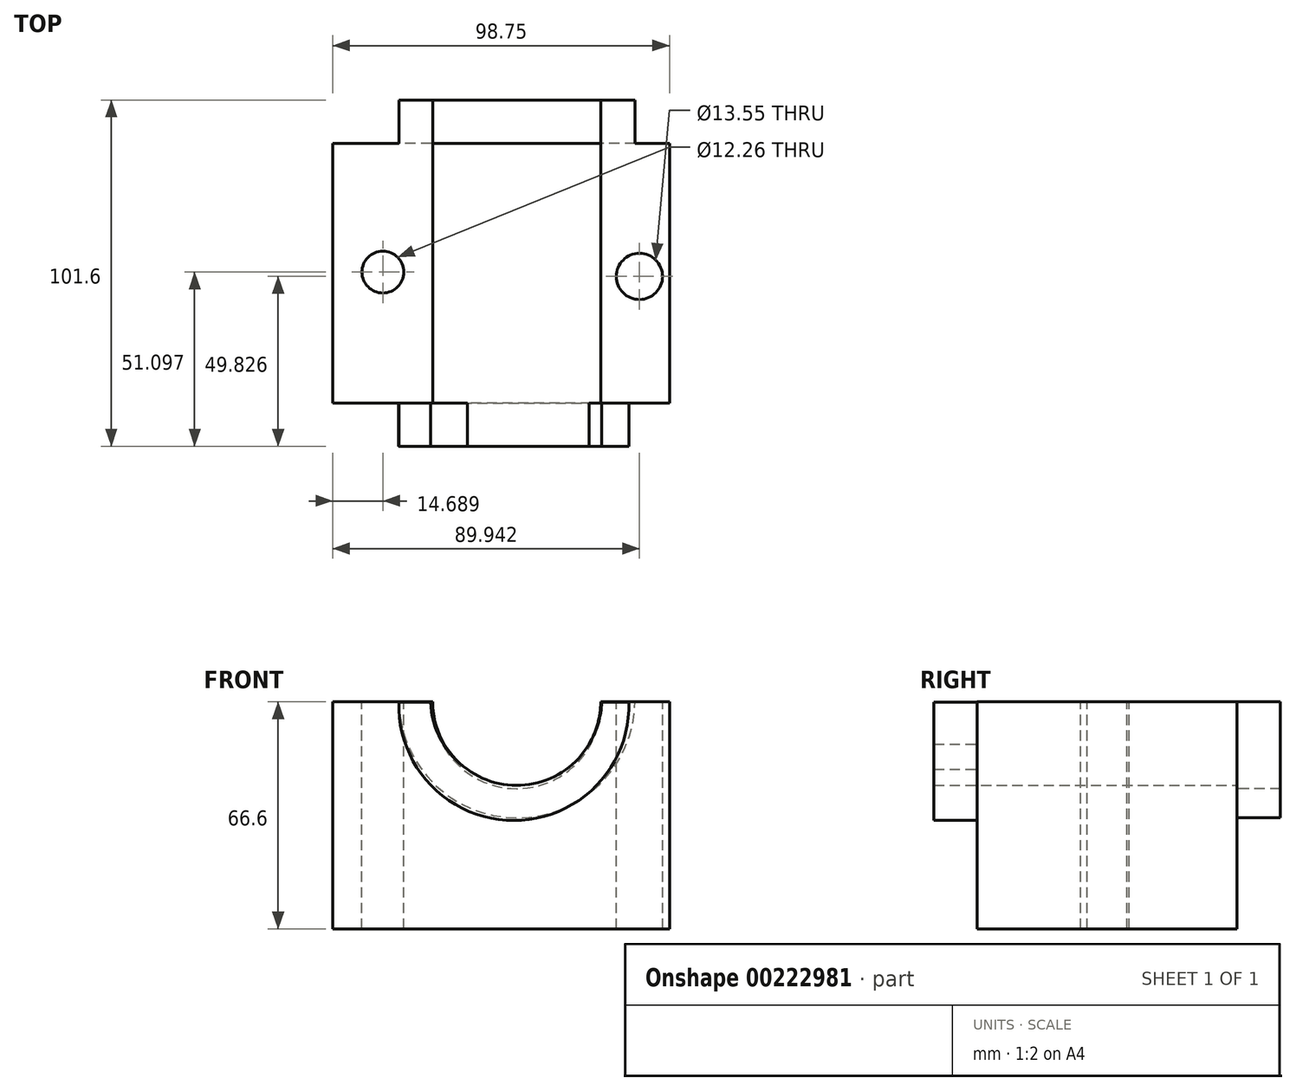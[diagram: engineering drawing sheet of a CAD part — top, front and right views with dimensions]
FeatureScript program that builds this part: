
annotation { "Feature Type Name" : "Feature", "Feature Type Description" : "" }
export const myFeature = defineFeature(function(context is Context, id is Id, definition is map)
    precondition{}
    {
        {
            var Q0;
            Q0=qCreatedBy(makeId("Front.planeOp"),FACE);
            var sketch = newSketch(context, id + "F0", { "sketchPlane" : qUnion([Q0])});
            skLineSegment(sketch, "E0.bottom", {"start": v(32.3, -49.6) * mm, "end": v(-66.44, -49.6) * mm});
            skLineSegment(sketch, "E0.top", {"start": v(32.3, 17) * mm, "end": v(-66.44, 17) * mm});
            skLineSegment(sketch, "E0.left", {"start": v(32.3, -49.6) * mm, "end": v(32.3, 17) * mm});
            skLineSegment(sketch, "E0.right", {"start": v(-66.44, -49.6) * mm, "end": v(-66.44, 17) * mm});
            skSolve(sketch);
        }
        {
            var Q0;
            Q0 = qSketchRegion(id + "F0", true);
            extrude(context, id + "F1", {"entities" : qUnion([Q0]), "oppositeDirection" : true, "depth" : 76.2 * mm});
        }
        {
            var Q0;
            Q0=makeQuery(id+"F1.opExtrude","CAP_FACE",FACE,{"disambiguationData":[OSD([sQuery(id+"F0.wireOp",EDGE,"E0.bottom"),sQuery(id+"F0.wireOp",EDGE,"E0.top"),sQuery(id+"F0.wireOp",EDGE,"E0.left"),sQuery(id+"F0.wireOp",EDGE,"E0.right")])],"isStart":true});
            var sketch = newSketch(context, id + "F2", { "sketchPlane" : qUnion([Q0])});
            skSolve(sketch);
        }
        {
            var Q0;
            Q0=makeQuery(id+"F2.imprint","IMPRINT",FACE,{"disambiguationData":[TD([[makeQuery(id+"F2.imprint","IMPRINT",EDGE,{"derivedFrom":makeQuery(id+"F1.opExtrude","CAP_EDGE",EDGE,{"disambiguationData":[OSD([sQuery(id+"F0.wireOp",EDGE,"E0.bottom")])],"isStart":true})}),-1.0]])]});
            var sketch = newSketch(context, id + "F3", { "sketchPlane" : qUnion([Q0])});
            skLineSegment(sketch, "E1", {"start": v(-37.75, 16.91) * mm, "end": v(-47.07, 16.91) * mm});
            skLineSegment(sketch, "E2", {"start": v(-47.07, 16.91) * mm, "end": v(-37.75, 16.91) * mm});
            skLineSegment(sketch, "E3", {"start": v(12.44, 16.91) * mm, "end": v(20.38, 16.91) * mm});
            skLineSegment(sketch, "E4", {"start": v(20.38, 16.91) * mm, "end": v(12.44, 16.91) * mm});
            skArc(sketch, "E5", {"start": v(-47.07, 16.91) * mm, "mid": v(-13.34, -17.83) * mm, "end": v(20.38, 16.91) * mm});
            skArc(sketch, "E6", {"start": v(-37.75, 16.91) * mm, "mid": v(-12.65, -7.34) * mm, "end": v(12.44, 16.91) * mm});
            skSolve(sketch);
        }
        {
            var Q0;
            Q0 = qSketchRegion(id + "F3", true);
            extrude(context, id + "F4", {"entities" : qUnion([Q0]), "operationType" : NewBodyOperationType.ADD, "depth" : 12.7 * mm});
        }
        {
            var Q0;
            Q0=qCreatedBy(makeId("Front.planeOp"),FACE);
            var sketch = newSketch(context, id + "F5", { "sketchPlane" : qUnion([Q0])});
            skCircle(sketch, "E7", {"center": v(-12.51, 17.09) * mm, "radius": 24.64 * mm});
            skSolve(sketch);
        }
        {
            var Q0;
            Q0 = qSketchRegion(id + "F5", true);
            extrude(context, id + "F6", {"entities" : qUnion([Q0]), "operationType" : NewBodyOperationType.REMOVE, "depth" : 12.7 * mm, "hasSecondDirection" : true, "secondDirectionOppositeDirection" : true, "secondDirectionDepth" : 88.9 * mm});
        }
        {
            var Q0;
            {var subQ1=sQuery(id+"F0.wireOp",EDGE,"E0.left");var subQ2=sQuery(id+"F0.wireOp",EDGE,"E0.top");Q0=makeQuery(id+"F6.boolean.opBoolean","SPLIT",FACE,{"disambiguationData":[TD([makeQuery(id+"F1.opExtrude","SWEPT_FACE",FACE,{"disambiguationData":[OSD([subQ1])]})])],"derivedFrom":makeQuery(id+"F1.opExtrude","SWEPT_FACE",FACE,{"disambiguationData":[OSD([subQ2])]})});}
            var sketch = newSketch(context, id + "F7", { "sketchPlane" : qUnion([Q0])});
            skCircle(sketch, "E8", {"center": v(23.5, 37.13) * mm, "radius": 6.78 * mm});
            skCircle(sketch, "E9", {"center": v(-51.75, 38.4) * mm, "radius": 6.13 * mm});
            skSolve(sketch);
        }
        {
            var Q0;
            Q0 = qSketchRegion(id + "F7", true);
            extrude(context, id + "F8", {"entities" : qUnion([Q0]), "operationType" : NewBodyOperationType.REMOVE, "endBound" : BoundingType.THROUGH_ALL, "oppositeDirection" : true, "depth" : 25.4 * mm});
        }
        {
            var Q0;
            Q0=makeQuery(id+"F1.opExtrude","CAP_FACE",FACE,{"disambiguationData":[OSD([sQuery(id+"F0.wireOp",EDGE,"E0.bottom"),sQuery(id+"F0.wireOp",EDGE,"E0.top"),sQuery(id+"F0.wireOp",EDGE,"E0.left"),sQuery(id+"F0.wireOp",EDGE,"E0.right")])],"isStart":false});
            var sketch = newSketch(context, id + "F9", { "sketchPlane" : qUnion([Q0])});
            skLineSegment(sketch, "E10", {"start": v(-12.12, 17) * mm, "end": v(-22.22, 17) * mm});
            skLineSegment(sketch, "E11", {"start": v(-22.22, 17) * mm, "end": v(-12.12, 17) * mm});
            skLineSegment(sketch, "E12", {"start": v(37.15, 17) * mm, "end": v(47.03, 17) * mm});
            skLineSegment(sketch, "E13", {"start": v(47.03, 17) * mm, "end": v(37.15, 17) * mm});
            skArc(sketch, "E14", {"start": v(-12.12, 17) * mm, "mid": v(12.51, -8.5) * mm, "end": v(37.15, 17) * mm});
            skArc(sketch, "E15", {"start": v(-22.22, 17) * mm, "mid": v(12.4, -17.06) * mm, "end": v(47.03, 17) * mm});
            skSolve(sketch);
        }
        {
            var Q0;
            Q0 = qSketchRegion(id + "F9", true);
            extrude(context, id + "F10", {"entities" : qUnion([Q0]), "operationType" : NewBodyOperationType.ADD, "depth" : 12.7 * mm});
        }
    });
